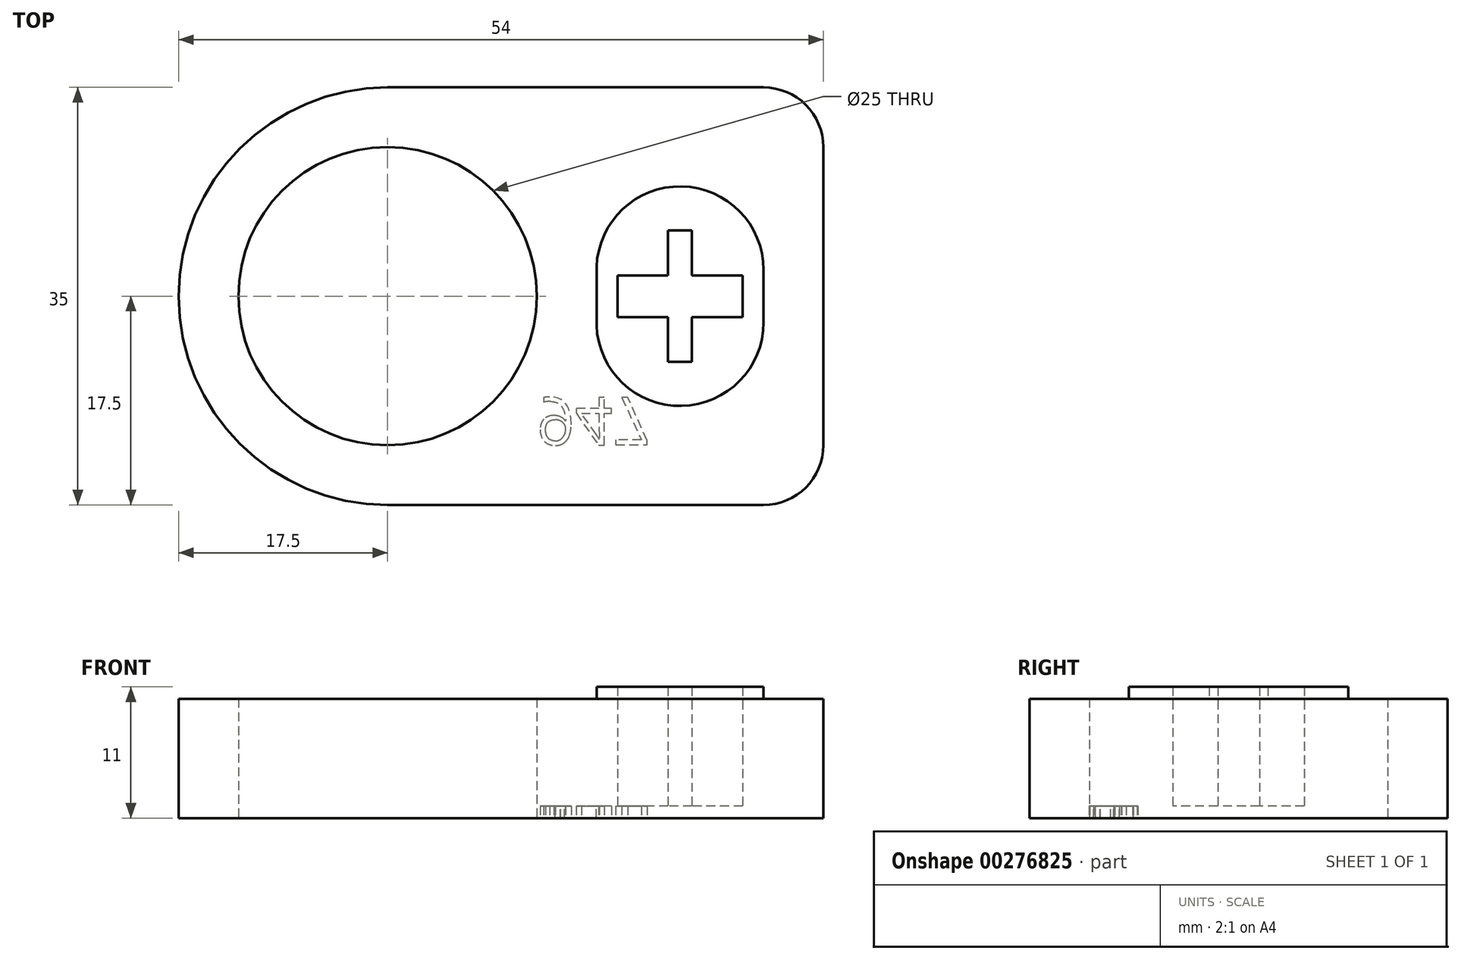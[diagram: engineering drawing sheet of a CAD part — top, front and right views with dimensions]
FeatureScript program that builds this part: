
annotation { "Feature Type Name" : "Feature", "Feature Type Description" : "" }
export const myFeature = defineFeature(function(context is Context, id is Id, definition is map)
    precondition{}
    {
        {
            var Q0;
            Q0=qCreatedBy(makeId("Top.planeOp"),FACE);
            var sketch = newSketch(context, id + "F0", { "sketchPlane" : qUnion([Q0])});
            skLineSegment(sketch, "E0.bottom", {"start": v(17.5, 0) * mm, "end": v(49, 0) * mm});
            skLineSegment(sketch, "E0.top", {"start": v(17.5, 35) * mm, "end": v(49, 35) * mm});
            skLineSegment(sketch, "E0.left", {"start": v(0, 17.5) * mm, "end": v(0, 17.5) * mm});
            skLineSegment(sketch, "E0.right", {"start": v(54, 5) * mm, "end": v(54, 30) * mm});
            skLineSegment(sketch, "E1.bottom", {"start": v(0, 0) * mm, "end": v(17.5, 0) * mm, "construction": true});
            skLineSegment(sketch, "E1.top", {"start": v(0, 17.5) * mm, "end": v(17.5, 17.5) * mm, "construction": true});
            skLineSegment(sketch, "E1.left", {"start": v(0, 0) * mm, "end": v(0, 17.5) * mm, "construction": true});
            skLineSegment(sketch, "E1.right", {"start": v(17.5, 0) * mm, "end": v(17.5, 17.5) * mm, "construction": true});
            skCircle(sketch, "E2", {"center": v(17.5, 17.5) * mm, "radius": 12.5 * mm});
            skPoint(sketch, "E3.visualSharp", {"position": v(0, 0) * mm});
            skArc(sketch, "E3.filletArc", {"start": v(0, 17.5) * mm, "mid": v(5.13, 5.13) * mm, "end": v(17.5, 0) * mm});
            skPoint(sketch, "E4.visualSharp", {"position": v(0, 35) * mm});
            skArc(sketch, "E4.filletArc", {"start": v(17.5, 35) * mm, "mid": v(5.13, 29.87) * mm, "end": v(0, 17.5) * mm});
            skPoint(sketch, "E5.visualSharp", {"position": v(54, 35) * mm});
            skArc(sketch, "E5.filletArc", {"start": v(54, 30) * mm, "mid": v(52.54, 33.54) * mm, "end": v(49, 35) * mm});
            skPoint(sketch, "E6.visualSharp", {"position": v(54, 0) * mm});
            skArc(sketch, "E6.filletArc", {"start": v(49, 0) * mm, "mid": v(52.54, 1.46) * mm, "end": v(54, 5) * mm});
            skSolve(sketch);
        }
        {
            var Q0;
            Q0=makeQuery(id+"F0.imprint","IMPRINT",FACE,{"disambiguationData":[TD([[makeQuery(id+"F0.imprint","IMPRINT",EDGE,{"derivedFrom":sQuery(id+"F0.wireOp",EDGE,"E0.bottom")}),1.0]])]});
            extrude(context, id + "F1", {"entities" : qUnion([Q0]), "depth" : 10 * mm});
        }
        {
            var Q0;
            Q0=makeQuery(id+"F1.opExtrude","CAP_FACE",FACE,{"disambiguationData":[OSD([sQuery(id+"F0.wireOp",EDGE,"E0.bottom"),sQuery(id+"F0.wireOp",EDGE,"E0.top"),sQuery(id+"F0.wireOp",EDGE,"E0.right"),sQuery(id+"F0.wireOp",EDGE,"E2"),sQuery(id+"F0.wireOp",EDGE,"E3.filletArc"),sQuery(id+"F0.wireOp",EDGE,"E4.filletArc"),sQuery(id+"F0.wireOp",EDGE,"E5.filletArc"),sQuery(id+"F0.wireOp",EDGE,"E6.filletArc")])],"isStart":false});
            var sketch = newSketch(context, id + "F2", { "sketchPlane" : qUnion([Q0])});
            skLineSegment(sketch, "E7.bottom", {"start": v(0, 0) * mm, "end": v(42, 0) * mm, "construction": true});
            skLineSegment(sketch, "E7.top", {"start": v(0, 17.5) * mm, "end": v(42, 17.5) * mm, "construction": true});
            skLineSegment(sketch, "E7.left", {"start": v(0, 0) * mm, "end": v(0, 17.5) * mm, "construction": true});
            skLineSegment(sketch, "E7.right", {"start": v(42, 0) * mm, "end": v(42, 17.5) * mm, "construction": true});
            skLineSegment(sketch, "E8", {"start": v(42, 17.5) * mm, "end": v(42, 19.7) * mm, "construction": true});
            skLineSegment(sketch, "E9", {"start": v(35, 19.96) * mm, "end": v(35, 17.5) * mm});
            skLineSegment(sketch, "E10", {"start": v(42, 17.5) * mm, "end": v(51.13, 17.5) * mm, "construction": true});
            skLineSegment(sketch, "E11", {"start": v(49, 19.7) * mm, "end": v(49, 17.5) * mm});
            skArc(sketch, "E12.trimOffspring", {"start": v(49, 19.7) * mm, "mid": v(41.87, 26.7) * mm, "end": v(35, 19.44) * mm});
            skLineSegment(sketch, "E13.MirrorCS", {"start": v(35, 15.04) * mm, "end": v(35, 17.5) * mm});
            skArc(sketch, "E14.MirrorCS", {"start": v(49, 15.3) * mm, "mid": v(41.87, 8.3) * mm, "end": v(35, 15.56) * mm});
            skLineSegment(sketch, "E15.MirrorCS", {"start": v(49, 15.3) * mm, "end": v(49, 17.5) * mm});
            skLineSegment(sketch, "E16.bottom", {"start": v(43, 23) * mm, "end": v(41, 23) * mm});
            skLineSegment(sketch, "E16.top", {"start": v(43, 12) * mm, "end": v(41, 12) * mm});
            skLineSegment(sketch, "E16.left", {"start": v(43, 23) * mm, "end": v(43, 19.25) * mm});
            skLineSegment(sketch, "E16.right", {"start": v(41, 23) * mm, "end": v(41, 19.25) * mm});
            skPoint(sketch, "E16.middle", {"position": v(42, 17.5) * mm});
            skLineSegment(sketch, "E17.bottom", {"start": v(47.25, 19.25) * mm, "end": v(43, 19.25) * mm});
            skLineSegment(sketch, "E17.top", {"start": v(47.25, 15.75) * mm, "end": v(43, 15.75) * mm});
            skLineSegment(sketch, "E17.left", {"start": v(47.25, 19.25) * mm, "end": v(47.25, 15.75) * mm});
            skLineSegment(sketch, "E17.right", {"start": v(36.75, 19.25) * mm, "end": v(36.75, 15.75) * mm});
            skPoint(sketch, "E17.cornerSnap0", {"position": v(42, 19.25) * mm});
            skLineSegment(sketch, "E18.trimOffspring", {"start": v(41, 19.25) * mm, "end": v(36.75, 19.25) * mm});
            skLineSegment(sketch, "E19.trimOffspring", {"start": v(43, 15.75) * mm, "end": v(43, 12) * mm});
            skLineSegment(sketch, "E20.trimOffspring", {"start": v(41, 15.75) * mm, "end": v(36.75, 15.75) * mm});
            skLineSegment(sketch, "E21.trimOffspring", {"start": v(41, 15.75) * mm, "end": v(41, 12) * mm});
            skSolve(sketch);
        }
        {
            var Q0;
            {var subQ10=sQuery(id+"F2.wireOp",EDGE,"E11");Q0=makeQuery(id+"F2.imprint","IMPRINT",FACE,{"disambiguationData":[TD([[makeQuery(id+"F2.imprint","IMPRINT",EDGE,{"derivedFrom":subQ10}),-1.0]])]});}
            extrude(context, id + "F3", {"entities" : qUnion([Q0]), "operationType" : NewBodyOperationType.ADD, "depth" : 1 * mm});
        }
        {
            var Q0;
            Q0=makeQuery(id+"F3.boolean.opBoolean","SPLIT",FACE,{"disambiguationData":[TD([makeQuery(id+"F3.opExtrude","SWEPT_FACE",FACE,{"disambiguationData":[OSD([sQuery(id+"F2.wireOp",EDGE,"E16.bottom")])]})])],"derivedFrom":makeQuery(id+"F1.opExtrude","CAP_FACE",FACE,{"disambiguationData":[OSD([sQuery(id+"F0.wireOp",EDGE,"E0.bottom"),sQuery(id+"F0.wireOp",EDGE,"E0.top"),sQuery(id+"F0.wireOp",EDGE,"E0.right"),sQuery(id+"F0.wireOp",EDGE,"E2"),sQuery(id+"F0.wireOp",EDGE,"E3.filletArc"),sQuery(id+"F0.wireOp",EDGE,"E4.filletArc"),sQuery(id+"F0.wireOp",EDGE,"E5.filletArc"),sQuery(id+"F0.wireOp",EDGE,"E6.filletArc")])],"isStart":false})});
            extrude(context, id + "F4", {"entities" : qUnion([Q0]), "operationType" : NewBodyOperationType.REMOVE, "oppositeDirection" : true, "depth" : 9 * mm});
        }
        {
            var Q0;
            Q0=makeQuery(id+"F1.opExtrude","CAP_FACE",FACE,{"disambiguationData":[OSD([sQuery(id+"F0.wireOp",EDGE,"E0.bottom"),sQuery(id+"F0.wireOp",EDGE,"E0.top"),sQuery(id+"F0.wireOp",EDGE,"E0.right"),sQuery(id+"F0.wireOp",EDGE,"E2"),sQuery(id+"F0.wireOp",EDGE,"E3.filletArc"),sQuery(id+"F0.wireOp",EDGE,"E4.filletArc"),sQuery(id+"F0.wireOp",EDGE,"E5.filletArc"),sQuery(id+"F0.wireOp",EDGE,"E6.filletArc")])],"isStart":true});
            var sketch = newSketch(context, id + "F5", { "sketchPlane" : qUnion([Q0])});
            skLineSegment(sketch, "E22.bottom", {"start": v(0, 0) * mm, "end": v(30, 0) * mm, "construction": true});
            skLineSegment(sketch, "E22.top", {"start": v(0, -5) * mm, "end": v(30, -5) * mm, "construction": true});
            skLineSegment(sketch, "E22.left", {"start": v(0, 0) * mm, "end": v(0, -5) * mm, "construction": true});
            skLineSegment(sketch, "E22.right", {"start": v(30, 0) * mm, "end": v(30, -5) * mm, "construction": true});
            skText(sketch, "E23", { "text": "947", "fontName": "OpenSans-Regular.ttf"});
            const initialGuessF5  = {"E23": [0.03, -0.009, 1, 0, 0.004]};
            skSetInitialGuess(sketch, initialGuessF5);
            skSolve(sketch);
        }
        {
            var Q0;
            Q0 = qSketchRegion(id + "F5", true);
            extrude(context, id + "F6", {"entities" : qUnion([Q0]), "operationType" : NewBodyOperationType.REMOVE, "oppositeDirection" : true, "depth" : 1 * mm});
        }
    });
